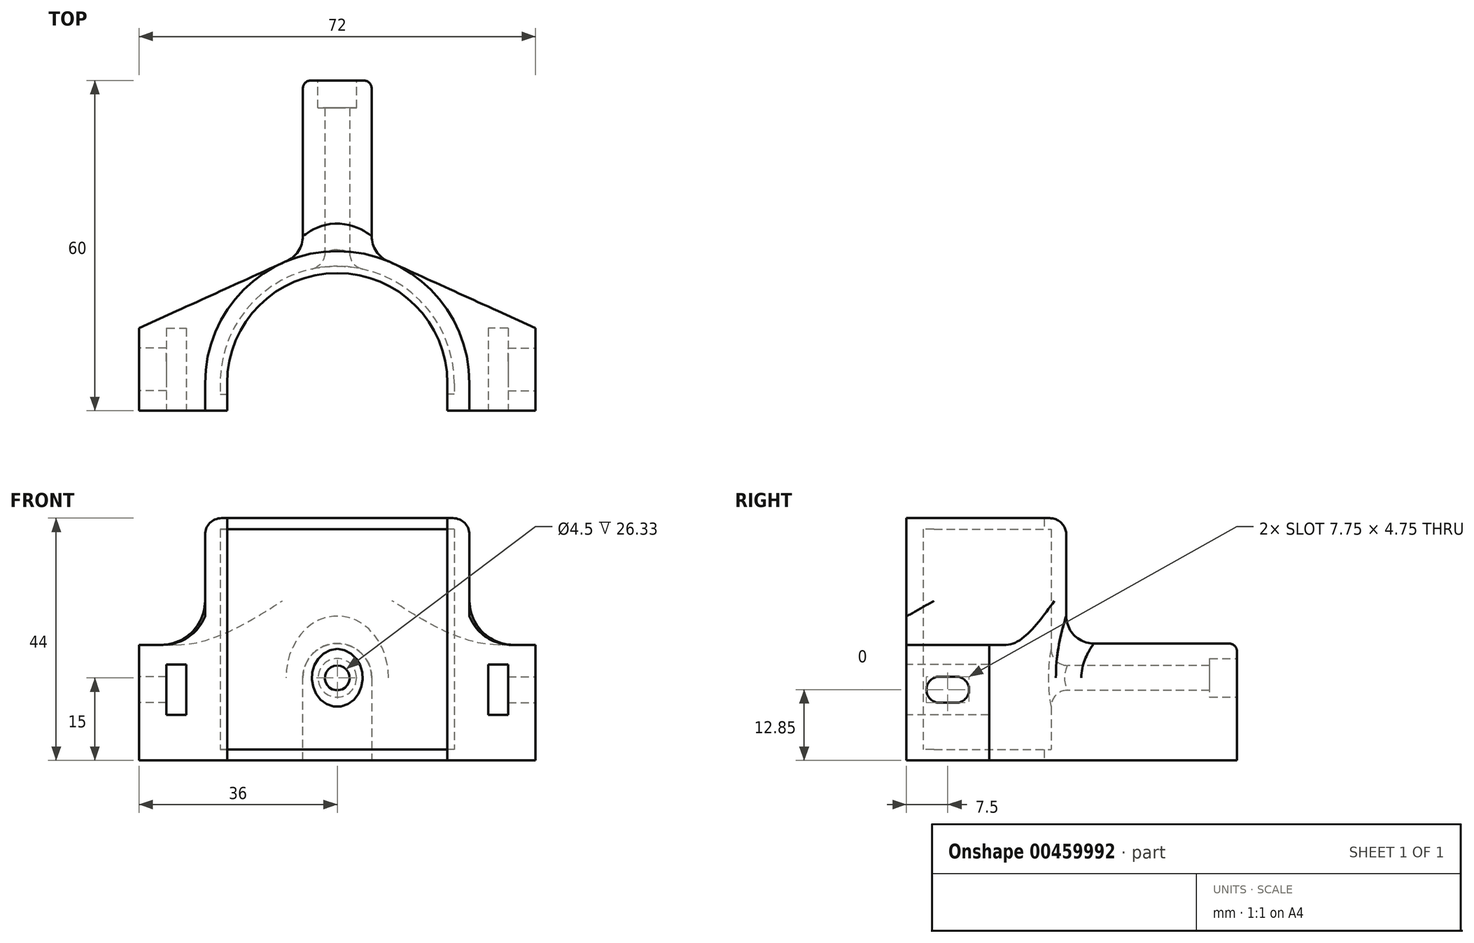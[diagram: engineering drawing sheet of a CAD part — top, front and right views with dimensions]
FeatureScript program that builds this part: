
annotation { "Feature Type Name" : "Feature", "Feature Type Description" : "" }
export const myFeature = defineFeature(function(context is Context, id is Id, definition is map)
    precondition{}
    {
        {
            var Q0;
            Q0=qCreatedBy(makeId("Top.planeOp"),FACE);
            var sketch = newSketch(context, id + "F0", { "sketchPlane" : qUnion([Q0])});
            skArc(sketch, "E0", {"start": v(20, 0) * mm, "mid": v(0, 20) * mm, "end": v(-20, 0) * mm});
            skArc(sketch, "E1", {"start": v(24, 0) * mm, "mid": v(0, 24) * mm, "end": v(-24, 0) * mm});
            skLineSegment(sketch, "E2.bottom", {"start": v(-24, 0) * mm, "end": v(-20, 0) * mm});
            skLineSegment(sketch, "E2.top", {"start": v(-24, -5) * mm, "end": v(-20, -5) * mm});
            skLineSegment(sketch, "E2.left", {"start": v(-24, 0) * mm, "end": v(-24, -5) * mm});
            skLineSegment(sketch, "E2.right", {"start": v(-20, 0) * mm, "end": v(-20, -5) * mm});
            skLineSegment(sketch, "E3.bottom", {"start": v(20, 0) * mm, "end": v(24, 0) * mm});
            skLineSegment(sketch, "E3.top", {"start": v(20, -5) * mm, "end": v(24, -5) * mm});
            skLineSegment(sketch, "E3.left", {"start": v(20, 0) * mm, "end": v(20, -5) * mm});
            skLineSegment(sketch, "E3.right", {"start": v(24, 0) * mm, "end": v(24, -5) * mm});
            skSolve(sketch);
        }
        {
            var Q0;
            Q0 = qSketchRegion(id + "F0", true);
            extrude(context, id + "F1", {"entities" : qUnion([Q0]), "depth" : 24 * mm, "offsetDistance" : 25 * mm, "hasSecondDirection" : true, "secondDirectionOppositeDirection" : true, "secondDirectionDepth" : 20 * mm});
        }
        {
            var Q0;
            Q0=qCreatedBy(makeId("Top.planeOp"),FACE);
            var sketch = newSketch(context, id + "F2", { "sketchPlane" : qUnion([Q0])});
            skArc(sketch, "E4", {"start": v(20, 0) * mm, "mid": v(0, 20) * mm, "end": v(-20, 0) * mm});
            skArc(sketch, "E5", {"start": v(21.25, 0) * mm, "mid": v(0, 21.25) * mm, "end": v(-21.25, 0) * mm});
            skLineSegment(sketch, "E6.bottom", {"start": v(-21.25, 0) * mm, "end": v(-20, 0) * mm});
            skLineSegment(sketch, "E6.top", {"start": v(-21.25, -2) * mm, "end": v(-20, -2) * mm});
            skLineSegment(sketch, "E6.left", {"start": v(-21.25, 0) * mm, "end": v(-21.25, -2) * mm});
            skLineSegment(sketch, "E6.right", {"start": v(-20, 0) * mm, "end": v(-20, -2) * mm});
            skLineSegment(sketch, "E7.bottom", {"start": v(21.25, 0) * mm, "end": v(20, 0) * mm});
            skLineSegment(sketch, "E7.top", {"start": v(21.25, -2) * mm, "end": v(20, -2) * mm});
            skLineSegment(sketch, "E7.left", {"start": v(21.25, 0) * mm, "end": v(21.25, -2) * mm});
            skLineSegment(sketch, "E7.right", {"start": v(20, 0) * mm, "end": v(20, -2) * mm});
            skPoint(sketch, "E8", {"position": v(0, 21.25) * mm});
            skSolve(sketch);
        }
        {
            var Q0;
            Q0 = qSketchRegion(id + "F2", true);
            extrude(context, id + "F3", {"entities" : qUnion([Q0]), "operationType" : NewBodyOperationType.REMOVE, "depth" : 22 * mm, "offsetDistance" : 25 * mm, "hasSecondDirection" : true, "secondDirectionOppositeDirection" : true, "secondDirectionDepth" : 18 * mm});
        }
        {
            var Q0;
            Q0=qCreatedBy(makeId("Top.planeOp"),FACE);
            var sketch = newSketch(context, id + "F4", { "sketchPlane" : qUnion([Q0])});
            skLineSegment(sketch, "E9.bottom", {"start": v(-24, -5) * mm, "end": v(-36, -5) * mm});
            skLineSegment(sketch, "E9.top", {"start": v(-24, 10) * mm, "end": v(-36, 10) * mm, "construction": true});
            skLineSegment(sketch, "E9.left", {"start": v(-24, -5) * mm, "end": v(-24, 10) * mm, "construction": true});
            skLineSegment(sketch, "E9.right", {"start": v(-36, -5) * mm, "end": v(-36, 10) * mm});
            skLineSegment(sketch, "E10.bottom", {"start": v(24, -5) * mm, "end": v(36, -5) * mm});
            skLineSegment(sketch, "E10.top", {"start": v(24, 10) * mm, "end": v(36, 10) * mm, "construction": true});
            skLineSegment(sketch, "E10.left", {"start": v(24, -5) * mm, "end": v(24, 10) * mm, "construction": true});
            skLineSegment(sketch, "E10.right", {"start": v(36, -5) * mm, "end": v(36, 10) * mm});
            skLineSegment(sketch, "E11", {"start": v(-36, 10) * mm, "end": v(-9.93, 21.85) * mm});
            skLineSegment(sketch, "E12", {"start": v(36, 10) * mm, "end": v(9.93, 21.85) * mm});
            skArc(sketch, "E13", {"start": v(-9.93, 21.85) * mm, "mid": v(-20.27, 10.16) * mm, "end": v(-24, -5) * mm});
            skArc(sketch, "E14", {"start": v(24, -5) * mm, "mid": v(20.27, 10.16) * mm, "end": v(9.93, 21.85) * mm});
            skSolve(sketch);
        }
        {
            var Q0;
            Q0 = qSketchRegion(id + "F4", true);
            extrude(context, id + "F5", {"entities" : qUnion([Q0]), "operationType" : NewBodyOperationType.ADD, "oppositeDirection" : true, "depth" : 20 * mm, "offsetDistance" : 25 * mm, "hasSecondDirection" : true, "secondDirectionOppositeDirection" : false, "secondDirectionDepth" : 1 * mm});
        }
        {
            var Q0;
            Q0=makeQuery(id+"F5.boolean.opBoolean","INTERSECT",EDGE,{"derivedFrom":[makeQuery(id+"F1.opExtrude","SWEPT_FACE",FACE,{"disambiguationData":[OSD([sQuery(id+"F0.wireOp",EDGE,"E1")])]}),makeQuery(id+"F5.opExtrude","CAP_FACE",FACE,{"disambiguationData":[OSD([sQuery(id+"F4.wireOp",EDGE,"E9.bottom"),sQuery(id+"F4.wireOp",EDGE,"E9.right"),sQuery(id+"F4.wireOp",EDGE,"E11"),sQuery(id+"F4.wireOp",EDGE,"E13")])],"isStart":true})]});
            var Q1;
            Q1=makeQuery(id+"F5.boolean.opBoolean","INTERSECT",EDGE,{"derivedFrom":[makeQuery(id+"F1.opExtrude","SWEPT_FACE",FACE,{"disambiguationData":[OSD([sQuery(id+"F0.wireOp",EDGE,"E1")])]}),makeQuery(id+"F5.opExtrude","CAP_FACE",FACE,{"disambiguationData":[OSD([sQuery(id+"F4.wireOp",EDGE,"E10.bottom"),sQuery(id+"F4.wireOp",EDGE,"E10.right"),sQuery(id+"F4.wireOp",EDGE,"E12"),sQuery(id+"F4.wireOp",EDGE,"E14")])],"isStart":true})]});
            fillet(context, id + "F6", {"entities" : qUnion([Q0, Q1]), "radius" : 8 * mm, "allowEdgeOverflow" : false});
        }
        {
            var Q0;
            Q0=makeQuery(id+"F1.opExtrude","CAP_EDGE",EDGE,{"disambiguationData":[OSD([sQuery(id+"F0.wireOp",EDGE,"E1")])],"isStart":false});
            fillet(context, id + "F7", {"entities" : qUnion([Q0]), "radius" : 3 * mm, "tangentPropagation" : true, "allowEdgeOverflow" : false});
        }
        {
            var Q0;
            Q0=makeQuery(id+"F5.boolean.opBoolean","MERGE",FACE,{"derivedFrom":[makeQuery(id+"F1.opExtrude","SWEPT_FACE",FACE,{"disambiguationData":[OSD([sQuery(id+"F0.wireOp",EDGE,"E2.top")])]}),makeQuery(id+"F5.opExtrude","SWEPT_FACE",FACE,{"disambiguationData":[OSD([sQuery(id+"F4.wireOp",EDGE,"E9.bottom")])]})]});
            var sketch = newSketch(context, id + "F8", { "sketchPlane" : qUnion([Q0])});
            skLineSegment(sketch, "E15.bottom", {"start": v(-31, -11.71) * mm, "end": v(-27.4, -11.71) * mm});
            skLineSegment(sketch, "E15.top", {"start": v(-31, -2.59) * mm, "end": v(-27.4, -2.59) * mm});
            skLineSegment(sketch, "E15.left", {"start": v(-31, -11.71) * mm, "end": v(-31, -2.59) * mm});
            skLineSegment(sketch, "E15.right", {"start": v(-27.4, -11.71) * mm, "end": v(-27.4, -2.59) * mm});
            skLineSegment(sketch, "E16.bottom", {"start": v(31, -11.71) * mm, "end": v(27.4, -11.71) * mm});
            skLineSegment(sketch, "E16.top", {"start": v(31, -2.59) * mm, "end": v(27.4, -2.59) * mm});
            skLineSegment(sketch, "E16.left", {"start": v(31, -11.71) * mm, "end": v(31, -2.59) * mm});
            skLineSegment(sketch, "E16.right", {"start": v(27.4, -11.71) * mm, "end": v(27.4, -2.59) * mm});
            skLineSegment(sketch, "E17", {"start": v(-31, -7.15) * mm, "end": v(-36, -7.15) * mm, "construction": true});
            skLineSegment(sketch, "E18", {"start": v(31, -7.15) * mm, "end": v(36, -7.15) * mm, "construction": true});
            skLineSegment(sketch, "E19", {"start": v(-29.2, -11.71) * mm, "end": v(-29.2, -20) * mm, "construction": true});
            skLineSegment(sketch, "E20", {"start": v(29.2, -11.71) * mm, "end": v(29.2, -20) * mm, "construction": true});
            skSolve(sketch);
        }
        {
            var Q0;
            Q0=makeQuery(id+"F8.imprint","IMPRINT",FACE,{"disambiguationData":[TD([[makeQuery(id+"F8.imprint","IMPRINT",EDGE,{"derivedFrom":sQuery(id+"F8.wireOp",EDGE,"E15.bottom")}),1.0]])]});
            var Q1;
            Q1=makeQuery(id+"F8.imprint","IMPRINT",FACE,{"disambiguationData":[TD([[makeQuery(id+"F8.imprint","IMPRINT",EDGE,{"derivedFrom":sQuery(id+"F8.wireOp",EDGE,"E16.bottom")}),-1.0]])]});
            extrude(context, id + "F9", {"entities" : qUnion([Q0, Q1]), "operationType" : NewBodyOperationType.REMOVE, "oppositeDirection" : true, "depth" : 15 * mm, "offsetDistance" : 25 * mm});
        }
        {
            var Q0;
            Q0=makeQuery(id+"F5.opExtrude","SWEPT_FACE",FACE,{"disambiguationData":[OSD([sQuery(id+"F4.wireOp",EDGE,"E9.right")])]});
            var sketch = newSketch(context, id + "F10", { "sketchPlane" : qUnion([Q0])});
            skLineSegment(sketch, "E21.bottom", {"start": v(-4, -4.78) * mm, "end": v(-1, -4.78) * mm});
            skLineSegment(sketch, "E21.top", {"start": v(-4, -9.53) * mm, "end": v(-1, -9.53) * mm});
            skLineSegment(sketch, "E21.left", {"start": v(-4, -4.78) * mm, "end": v(-4, -9.53) * mm});
            skLineSegment(sketch, "E21.right", {"start": v(-1, -4.78) * mm, "end": v(-1, -9.52) * mm});
            skArc(sketch, "E22", {"start": v(-4, -4.78) * mm, "mid": v(-6.38, -7.15) * mm, "end": v(-4, -9.53) * mm});
            skArc(sketch, "E23", {"start": v(-1, -9.53) * mm, "mid": v(1.37, -7.15) * mm, "end": v(-1, -4.78) * mm});
            skLineSegment(sketch, "E24", {"start": v(5, -2.59) * mm, "end": v(5, -11.71) * mm, "construction": true});
            skPoint(sketch, "E25", {"position": v(5, -7.15) * mm});
            skPoint(sketch, "E26", {"position": v(-2.5, -4.78) * mm});
            skSolve(sketch);
        }
        {
            var Q0;
            Q0 = qSketchRegion(id + "F10", true);
            extrude(context, id + "F11", {"entities" : qUnion([Q0]), "operationType" : NewBodyOperationType.REMOVE, "endBound" : BoundingType.UP_TO_NEXT, "oppositeDirection" : true, "depth" : 25 * mm, "offsetDistance" : 25 * mm});
        }
        {
            var Q0;
            Q0=makeQuery(id+"F5.opExtrude","SWEPT_FACE",FACE,{"disambiguationData":[OSD([sQuery(id+"F4.wireOp",EDGE,"E10.right")])]});
            var sketch = newSketch(context, id + "F12", { "sketchPlane" : qUnion([Q0])});
            skLineSegment(sketch, "E27.bottom", {"start": v(1, -4.78) * mm, "end": v(4, -4.78) * mm});
            skLineSegment(sketch, "E27.top", {"start": v(1, -9.53) * mm, "end": v(4, -9.53) * mm});
            skLineSegment(sketch, "E27.left", {"start": v(1, -4.78) * mm, "end": v(1, -9.53) * mm});
            skLineSegment(sketch, "E27.right", {"start": v(4, -4.78) * mm, "end": v(4, -9.53) * mm});
            skArc(sketch, "E28", {"start": v(1, -4.78) * mm, "mid": v(-1.37, -7.15) * mm, "end": v(1, -9.53) * mm});
            skArc(sketch, "E29", {"start": v(4, -9.53) * mm, "mid": v(6.38, -7.15) * mm, "end": v(4, -4.78) * mm});
            skSolve(sketch);
        }
        {
            var Q0;
            Q0 = qSketchRegion(id + "F12", true);
            extrude(context, id + "F13", {"entities" : qUnion([Q0]), "operationType" : NewBodyOperationType.REMOVE, "endBound" : BoundingType.UP_TO_NEXT, "oppositeDirection" : true, "depth" : 25 * mm, "offsetDistance" : 25 * mm});
        }
        {
            var Q0;
            Q0=qCreatedBy(makeId("Front.planeOp"),FACE);
            cPlane(context, id + "F14", {"entities" : qUnion([Q0]), "cplaneType" : CPlaneType.OFFSET, "offset" : 22 * mm, "oppositeDirection" : true, "width" : 150 * mm, "height" : 150 * mm});
        }
        {
            var Q0;
            Q0=qCreatedBy(id+"F14.planeOp",FACE);
            var sketch = newSketch(context, id + "F15", { "sketchPlane" : qUnion([Q0])});
            skLineSegment(sketch, "E30.bottom", {"start": v(-6.25, -20) * mm, "end": v(6.25, -20) * mm});
            skLineSegment(sketch, "E30.top", {"start": v(-6.25, -5) * mm, "end": v(6.25, -5) * mm});
            skLineSegment(sketch, "E30.left", {"start": v(-6.25, -20) * mm, "end": v(-6.25, -5) * mm});
            skLineSegment(sketch, "E30.right", {"start": v(6.25, -20) * mm, "end": v(6.25, -5) * mm});
            skArc(sketch, "E31", {"start": v(6.25, -5) * mm, "mid": v(0, 1.25) * mm, "end": v(-6.25, -5) * mm});
            skLineSegment(sketch, "E32", {"start": v(-6.25, -12.5) * mm, "end": v(-9.93, -12.5) * mm, "construction": true});
            skLineSegment(sketch, "E33", {"start": v(6.25, -12.5) * mm, "end": v(9.93, -12.5) * mm, "construction": true});
            skCircle(sketch, "E34", {"center": v(0, -5) * mm, "radius": 2.25 * mm});
            skSolve(sketch);
        }
        {
            var Q0;
            Q0 = qSketchRegion(id + "F15", true);
            extrude(context, id + "F16", {"entities" : qUnion([Q0]), "operationType" : NewBodyOperationType.ADD, "oppositeDirection" : true, "depth" : 33 * mm, "offsetDistance" : 25 * mm});
        }
        {
            var Q0;
            Q0=makeQuery(id+"F16.opExtrude","CAP_FACE",FACE,{"disambiguationData":[OSD([sQuery(id+"F15.wireOp",EDGE,"E30.bottom"),sQuery(id+"F15.wireOp",EDGE,"E30.left"),sQuery(id+"F15.wireOp",EDGE,"E30.right"),sQuery(id+"F15.wireOp",EDGE,"E31"),sQuery(id+"F15.wireOp",EDGE,"E34")])],"isStart":false});
            var sketch = newSketch(context, id + "F17", { "sketchPlane" : qUnion([Q0])});
            skCircle(sketch, "E35", {"center": v(0, -5) * mm, "radius": 2.25 * mm});
            skSolve(sketch);
        }
        {
            var Q0;
            Q0 = qSketchRegion(id + "F17", true);
            extrude(context, id + "F18", {"entities" : qUnion([Q0]), "operationType" : NewBodyOperationType.REMOVE, "oppositeDirection" : true, "depth" : 40 * mm, "offsetDistance" : 25 * mm});
        }
        {
            var Q0;
            Q0=makeQuery(id+"F16.opExtrude","CAP_FACE",FACE,{"disambiguationData":[OSD([sQuery(id+"F15.wireOp",EDGE,"E30.bottom"),sQuery(id+"F15.wireOp",EDGE,"E30.left"),sQuery(id+"F15.wireOp",EDGE,"E30.right"),sQuery(id+"F15.wireOp",EDGE,"E31"),sQuery(id+"F15.wireOp",EDGE,"E34")])],"isStart":false});
            var sketch = newSketch(context, id + "F19", { "sketchPlane" : qUnion([Q0])});
            skCircle(sketch, "E36", {"center": v(0, -5) * mm, "radius": 3.5 * mm});
            skSolve(sketch);
        }
        {
            var Q0;
            Q0 = qSketchRegion(id + "F19", true);
            extrude(context, id + "F20", {"entities" : qUnion([Q0]), "operationType" : NewBodyOperationType.REMOVE, "oppositeDirection" : true, "depth" : 5 * mm, "offsetDistance" : 25 * mm});
        }
        {
            var Q0;
            Q0=makeQuery(id+"F20.boolean.opBoolean","COPY",EDGE,{"derivedFrom":makeQuery(id+"F20.opExtrude","CAP_EDGE",EDGE,{"disambiguationData":[OSD([sQuery(id+"F19.wireOp",EDGE,"E36")])],"isStart":true})});
            var Q1;
            Q1=makeQuery(id+"F16.opExtrude","CAP_EDGE",EDGE,{"disambiguationData":[OSD([sQuery(id+"F15.wireOp",EDGE,"E31")])],"isStart":false});
            fillet(context, id + "F21", {"entities" : qUnion([Q0, Q1]), "radius" : 1.5 * mm, "tangentPropagation" : true, "allowEdgeOverflow" : false});
        }
        {
            var Q0;
            Q0=makeQuery(id+"F18.boolean.opBoolean","INTERSECT",EDGE,{"derivedFrom":[makeQuery(id+"F3.boolean.opBoolean","COPY",FACE,{"derivedFrom":makeQuery(id+"F3.opExtrude","SWEPT_FACE",FACE,{"disambiguationData":[OSD([sQuery(id+"F2.wireOp",EDGE,"E5")])]})}),makeQuery(id+"F18.opExtrude","SWEPT_FACE",FACE,{"disambiguationData":[OSD([sQuery(id+"F17.wireOp",EDGE,"E35")])]})]});
            fillet(context, id + "F22", {"entities" : qUnion([Q0]), "radius" : 3 * mm, "tangentPropagation" : true, "allowEdgeOverflow" : false});
        }
        {
            var Q0;
            Q0=makeQuery(id+"F16.boolean.opBoolean","INTERSECT",EDGE,{"derivedFrom":[makeQuery(id+"F1.opExtrude","SWEPT_FACE",FACE,{"disambiguationData":[OSD([sQuery(id+"F0.wireOp",EDGE,"E1")])]}),makeQuery(id+"F16.opExtrude","SWEPT_FACE",FACE,{"disambiguationData":[OSD([sQuery(id+"F15.wireOp",EDGE,"E30.right")])]})]});
            fillet(context, id + "F23", {"entities" : qUnion([Q0]), "radius" : 5 * mm, "tangentPropagation" : true, "allowEdgeOverflow" : false});
        }
    });
